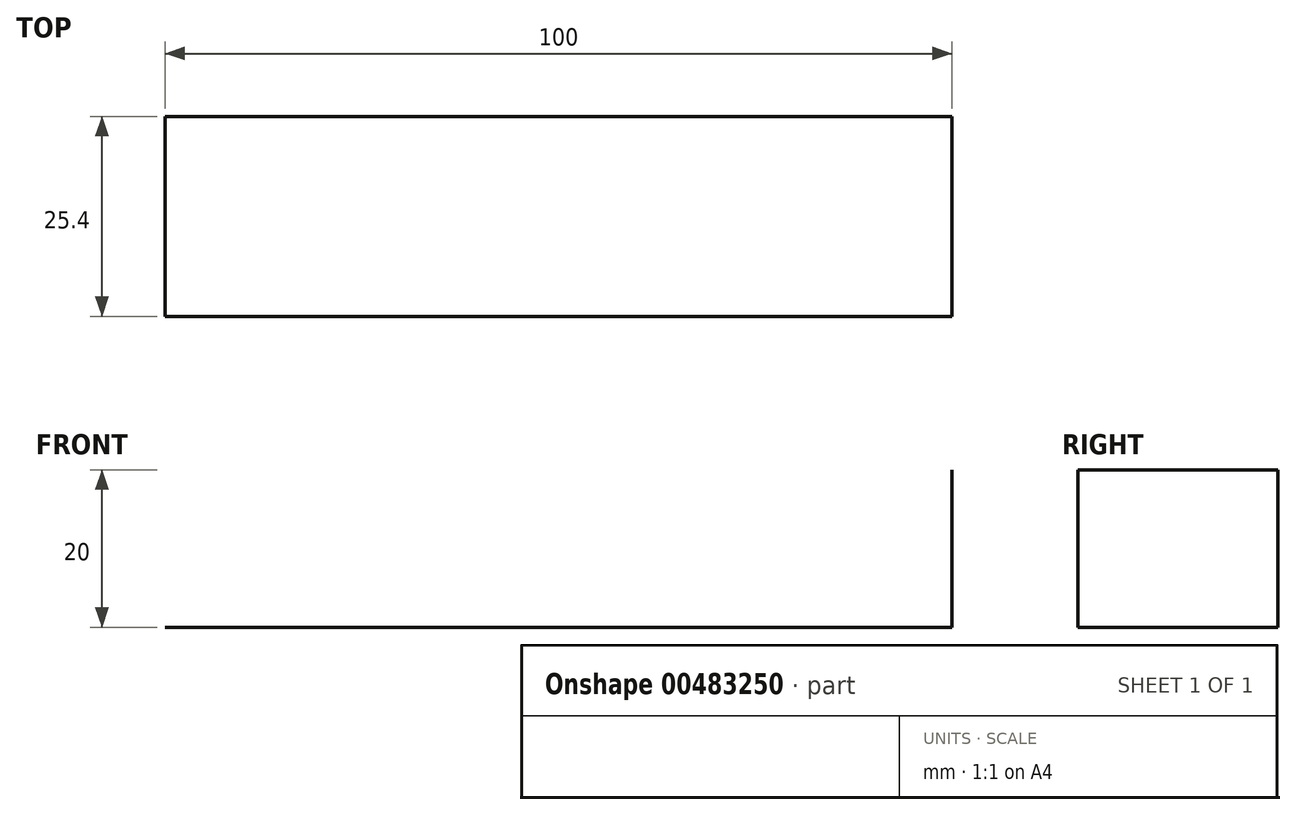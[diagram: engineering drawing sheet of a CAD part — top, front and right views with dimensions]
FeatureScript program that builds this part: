
annotation { "Feature Type Name" : "Feature", "Feature Type Description" : "" }
export const myFeature = defineFeature(function(context is Context, id is Id, definition is map)
    precondition{}
    {
        {
            var Q0;
            Q0=qCreatedBy(makeId("Front.planeOp"),FACE);
            var sketch = newSketch(context, id + "F0", { "sketchPlane" : qUnion([Q0])});
            skLineSegment(sketch, "E0", {"start": v(-50, 0) * mm, "end": v(50, 0) * mm});
            skLineSegment(sketch, "E1", {"start": v(50, 0) * mm, "end": v(50, 20) * mm});
            skSolve(sketch);
        }
        {
            var Q0;
            Q0=sQuery(id+"F0.wireOp",EDGE,"E0");
            var Q1;
            Q1=sQuery(id+"F0.wireOp",EDGE,"E1");
            extrude(context, id + "F1", {"bodyType" : ToolBodyType.SURFACE, "surfaceEntities" : qUnion([Q0, Q1]), "endBound" : BoundingType.SYMMETRIC, "depth" : 25.4 * mm});
        }
    });
